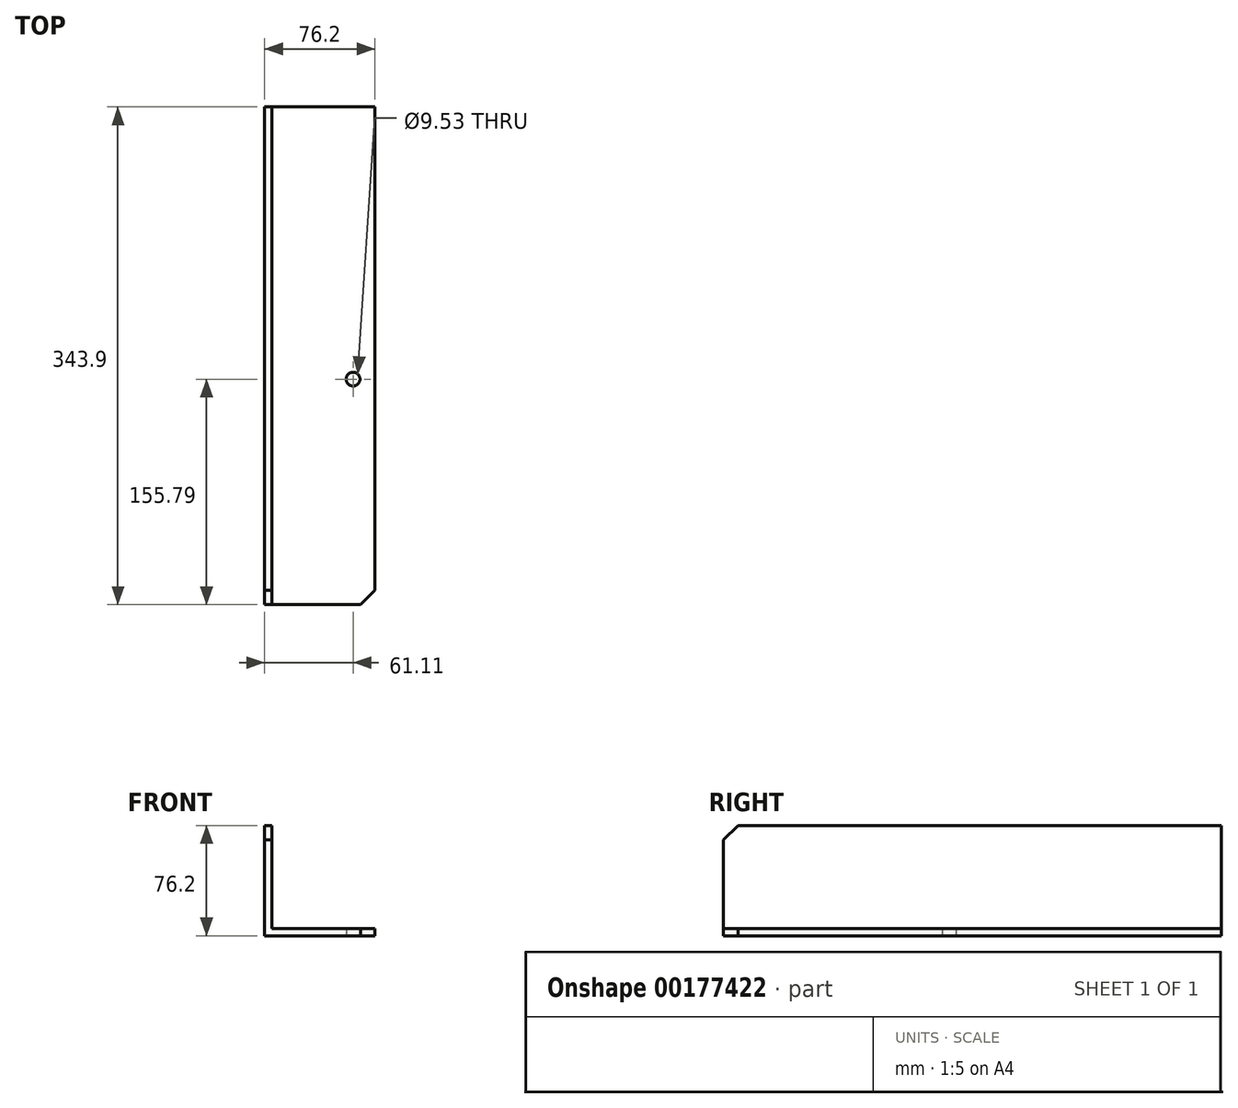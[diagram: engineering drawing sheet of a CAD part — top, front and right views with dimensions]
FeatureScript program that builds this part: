
annotation { "Feature Type Name" : "Feature", "Feature Type Description" : "" }
export const myFeature = defineFeature(function(context is Context, id is Id, definition is map)
    precondition{}
    {
        {
            var Q0;
            Q0=qCreatedBy(makeId("Front.planeOp"),FACE);
            var sketch = newSketch(context, id + "F0", { "sketchPlane" : qUnion([Q0])});
            skLineSegment(sketch, "E0", {"start": v(0, 0) * mm, "end": v(76.2, 0) * mm});
            skLineSegment(sketch, "E1", {"start": v(0, 0) * mm, "end": v(0, 76.2) * mm});
            skLineSegment(sketch, "E2.0", {"start": v(5, 5) * mm, "end": v(5, 76.2) * mm});
            skLineSegment(sketch, "E2.1", {"start": v(5, 5) * mm, "end": v(76.2, 5) * mm});
            skLineSegment(sketch, "E3", {"start": v(0, 76.2) * mm, "end": v(5, 76.2) * mm});
            skLineSegment(sketch, "E4", {"start": v(76.2, 0) * mm, "end": v(76.2, 5) * mm});
            skSolve(sketch);
        }
        {
            var Q0;
            Q0=makeQuery(id+"F0.imprint","IMPRINT",FACE,{"disambiguationData":[TD([[makeQuery(id+"F0.imprint","IMPRINT",EDGE,{"derivedFrom":sQuery(id+"F0.wireOp",EDGE,"E0")}),1.0]])]});
            extrude(context, id + "F1", {"entities" : qUnion([Q0]), "depth" : 343.9 * mm});
        }
        {
            var Q0;
            Q0=makeQuery(id+"F1.opExtrude","CAP_EDGE",EDGE,{"disambiguationData":[OSD([sQuery(id+"F0.wireOp",EDGE,"E4")])],"isStart":false});
            chamfer(context, id + "F2", {"entities" : qUnion([Q0]), "width" : 10 * mm, "tangentPropagation" : true});
        }
        {
            var Q0;
            Q0=makeQuery(id+"F1.opExtrude","CAP_EDGE",EDGE,{"disambiguationData":[OSD([sQuery(id+"F0.wireOp",EDGE,"E3")])],"isStart":false});
            chamfer(context, id + "F3", {"entities" : qUnion([Q0]), "width" : 10 * mm, "tangentPropagation" : true});
        }
        {
            var Q0;
            Q0=makeQuery(id+"F1.opExtrude","SWEPT_FACE",FACE,{"disambiguationData":[OSD([sQuery(id+"F0.wireOp",EDGE,"E0")])]});
            var sketch = newSketch(context, id + "F4", { "sketchPlane" : qUnion([Q0])});
            skLineSegment(sketch, "E5.0", {"start": v(0, 188.11) * mm, "end": v(66.2, 188.11) * mm});
            skLineSegment(sketch, "E6.0", {"start": v(71.2, 331.83) * mm, "end": v(64.13, 338.9) * mm});
            skLineSegment(sketch, "E6.1", {"start": v(71.2, 5) * mm, "end": v(71.2, 331.83) * mm});
            skLineSegment(sketch, "E6.2", {"start": v(64.13, 338.9) * mm, "end": v(5, 338.9) * mm});
            skLineSegment(sketch, "E6.3", {"start": v(5, 338.9) * mm, "end": v(5, 5) * mm});
            skLineSegment(sketch, "E6.4", {"start": v(5, 5) * mm, "end": v(71.2, 5) * mm});
            skLineSegment(sketch, "E7.0", {"start": v(61.1, 333.9) * mm, "end": v(61.1, 0) * mm});
            skPoint(sketch, "E8", {"position": v(61.1, 188.11) * mm});
            skSolve(sketch);
        }
        {
            var Q0;
            Q0=sQuery(id+"F4.wireOp",VERTEX,"E8");
            var Q1;
            Q1=makeQuery(id+"F1.opExtrude","SWEPT_BODY",BODY,{"disambiguationData":[OSD([sQuery(id+"F0.wireOp",EDGE,"E0"),sQuery(id+"F0.wireOp",EDGE,"E1"),sQuery(id+"F0.wireOp",EDGE,"E2.0"),sQuery(id+"F0.wireOp",EDGE,"E2.1"),sQuery(id+"F0.wireOp",EDGE,"E3"),sQuery(id+"F0.wireOp",EDGE,"E4")])]});
            hole(context, id + "F5", {"style" : HoleStyle.SIMPLE, "endStyle" : HoleEndStyle.THROUGH, "holeDiameter" : 9.53 * mm, "locations" : qUnion([Q0]), "scope" : qUnion([Q1]), "isTappedThrough" : true});
        }
    });
